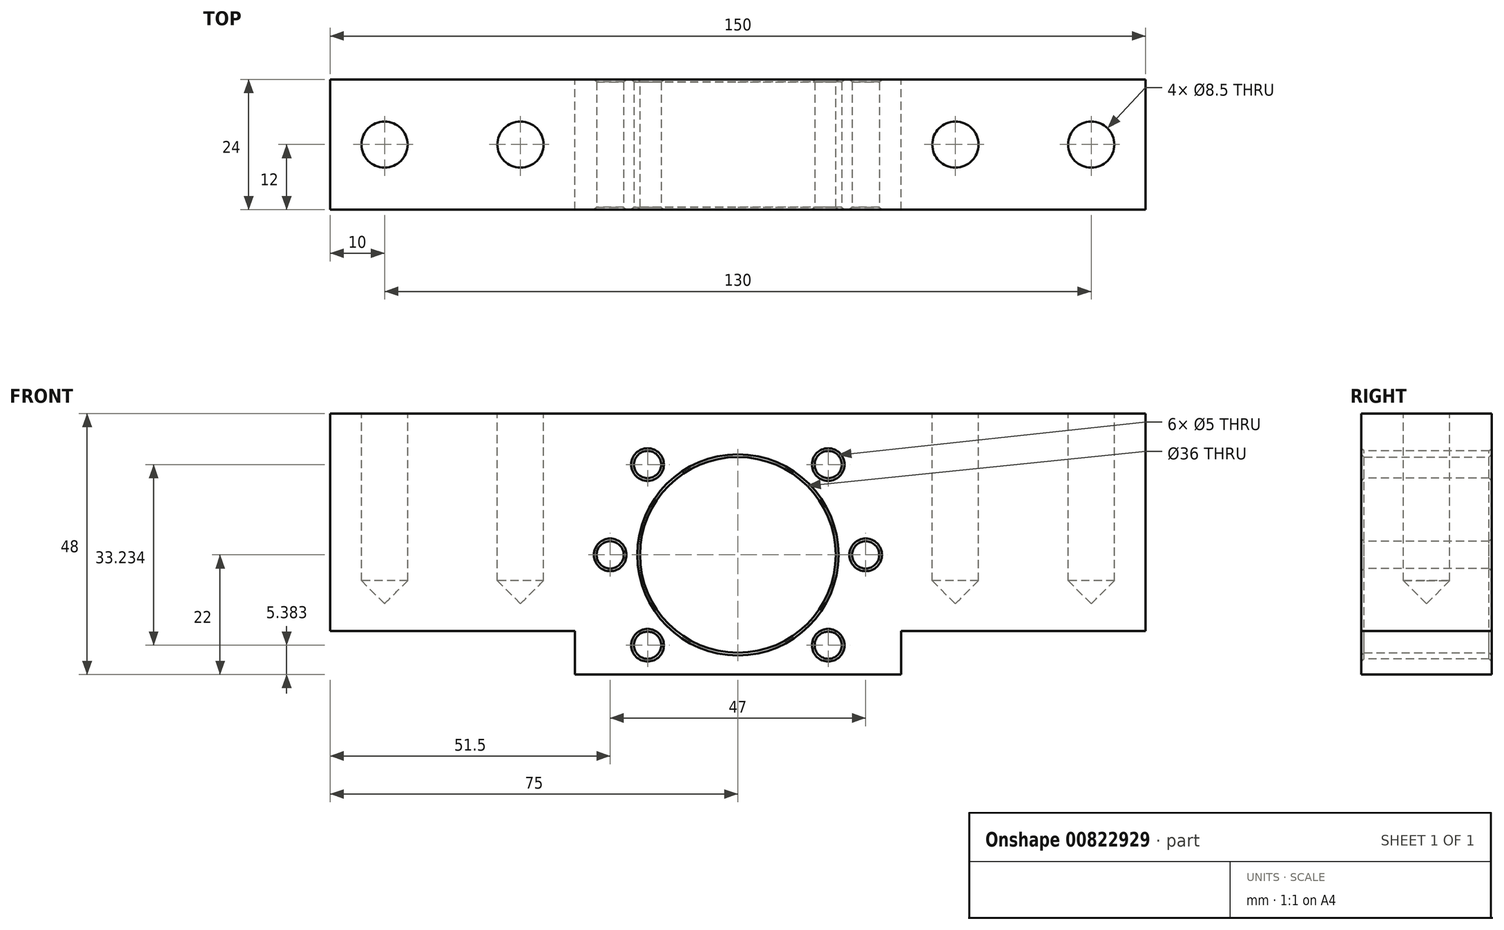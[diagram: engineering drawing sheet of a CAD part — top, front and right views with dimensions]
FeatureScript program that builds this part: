
annotation { "Feature Type Name" : "Feature", "Feature Type Description" : "" }
export const myFeature = defineFeature(function(context is Context, id is Id, definition is map)
    precondition{}
    {
        {
            var Q0;
            Q0=qCreatedBy(makeId("Front.planeOp"),FACE);
            var sketch = newSketch(context, id + "F0", { "sketchPlane" : qUnion([Q0])});
            skCircle(sketch, "E0", {"center": v(0, 0) * mm, "radius": 18 * mm});
            skArc(sketch, "E1", {"start": v(-18.9, 22) * mm, "mid": v(-29, 0) * mm, "end": v(-18.9, -22) * mm, "construction": true});
            skLineSegment(sketch, "E2", {"start": v(0, 0) * mm, "end": v(0, 12) * mm, "construction": true});
            skLineSegment(sketch, "E3", {"start": v(0, 12) * mm, "end": v(-93.5, 12) * mm, "construction": true});
            skLineSegment(sketch, "E4", {"start": v(-93.5, 36) * mm, "end": v(34.56, 36) * mm, "construction": true});
            skLineSegment(sketch, "E5", {"start": v(-93.5, 36) * mm, "end": v(-93.5, 12) * mm, "construction": true});
            skLineSegment(sketch, "E6", {"start": v(-105.7, -10) * mm, "end": v(69, -10) * mm, "construction": true});
            skCircle(sketch, "E7", {"center": v(0, 0) * mm, "radius": 10 * mm, "construction": true});
            skLineSegment(sketch, "E8.bottom", {"start": v(18.9, -22) * mm, "end": v(-18.9, -22) * mm, "construction": true});
            skLineSegment(sketch, "E8.top", {"start": v(18.9, 22) * mm, "end": v(-18.9, 22) * mm, "construction": true});
            skArc(sketch, "E9.trimOffspring", {"start": v(18.9, -22) * mm, "mid": v(29, 0) * mm, "end": v(18.9, 22) * mm, "construction": true});
            skPoint(sketch, "E10.orphan", {"position": v(29, 22) * mm});
            skLineSegment(sketch, "E11.bottom", {"start": v(30, -22) * mm, "end": v(-30, -22) * mm});
            skLineSegment(sketch, "E11.top", {"start": v(30, 30) * mm, "end": v(-30, 30) * mm, "construction": true});
            skLineSegment(sketch, "E11.left", {"start": v(30, -22) * mm, "end": v(30, 30) * mm, "construction": true});
            skLineSegment(sketch, "E11.right", {"start": v(-30, -22) * mm, "end": v(-30, 30) * mm, "construction": true});
            skPoint(sketch, "E11.middle", {"position": v(0, 4) * mm});
            skLineSegment(sketch, "E12", {"start": v(-30, -22) * mm, "end": v(-75, 26) * mm, "construction": true});
            skLineSegment(sketch, "E13", {"start": v(-75, 26) * mm, "end": v(-75, 50) * mm, "construction": true});
            skLineSegment(sketch, "E14", {"start": v(-75, 50) * mm, "end": v(0, 50) * mm, "construction": true});
            skLineSegment(sketch, "E15.MirrorCS", {"start": v(75, 50) * mm, "end": v(0, 50) * mm, "construction": true});
            skLineSegment(sketch, "E16.MirrorCS", {"start": v(75, 26) * mm, "end": v(75, 50) * mm, "construction": true});
            skLineSegment(sketch, "E17.MirrorCS", {"start": v(30, -22) * mm, "end": v(75, 26) * mm, "construction": true});
            skLineSegment(sketch, "E18", {"start": v(-75, 26) * mm, "end": v(75, 26) * mm});
            skLineSegment(sketch, "E19", {"start": v(-75, 26) * mm, "end": v(-75, -14) * mm});
            skLineSegment(sketch, "E20", {"start": v(-75, -14) * mm, "end": v(-30, -14) * mm});
            skLineSegment(sketch, "E21", {"start": v(75, -14) * mm, "end": v(75, 26) * mm});
            skLineSegment(sketch, "E22", {"start": v(-30, -22) * mm, "end": v(-30, -14) * mm});
            skLineSegment(sketch, "E23", {"start": v(30, -22) * mm, "end": v(30, -14) * mm});
            skLineSegment(sketch, "E24.trimOffspring", {"start": v(-25.4, -14) * mm, "end": v(25.4, -14) * mm, "construction": true});
            skLineSegment(sketch, "E25.trimOffspring", {"start": v(30, -14) * mm, "end": v(75, -14) * mm});
            skSolve(sketch);
        }
        {
            var Q0;
            Q0=qSketchRegion(id+"F0",true);
            extrude(context, id + "F1", {"entities" : qUnion([Q0]), "depth" : 24 * mm, "offsetDistance" : 25 * mm});
        }
        {
            var Q0;
            Q0=makeQuery(id+"F1.opExtrude","CAP_FACE",FACE,{"disambiguationData":[OSD([sQuery(id+"F0.wireOp",EDGE,"E0"),sQuery(id+"F0.wireOp",EDGE,"E11.bottom"),sQuery(id+"F0.wireOp",EDGE,"E12"),sQuery(id+"F0.wireOp",EDGE,"E13"),sQuery(id+"F0.wireOp",EDGE,"E14"),sQuery(id+"F0.wireOp",EDGE,"E15.MirrorCS"),sQuery(id+"F0.wireOp",EDGE,"E16.MirrorCS"),sQuery(id+"F0.wireOp",EDGE,"E17.MirrorCS")])],"isStart":false});
            var sketch = newSketch(context, id + "F2", { "sketchPlane" : qUnion([Q0])});
            skLineSegment(sketch, "E26", {"start": v(0, 0) * mm, "end": v(0, 38) * mm, "construction": true});
            skCircle(sketch, "E27", {"center": v(0, 0) * mm, "radius": 23.5 * mm, "construction": true});
            skLineSegment(sketch, "E28", {"start": v(0, 0) * mm, "end": v(-28.4, 0) * mm, "construction": true});
            skCircle(sketch, "E29", {"center": v(-23.5, 0) * mm, "radius": 2.5 * mm});
            skCircle(sketch, "E30.1.0", {"center": v(-16.62, -16.62) * mm, "radius": 2.5 * mm});
            skCircle(sketch, "E30.2.0", {"center": v(0, -23.5) * mm, "radius": 2.5 * mm, "construction": true});
            skCircle(sketch, "E30.3.0", {"center": v(16.62, -16.62) * mm, "radius": 2.5 * mm});
            skCircle(sketch, "E30.4.0", {"center": v(23.5, 0) * mm, "radius": 2.5 * mm});
            skCircle(sketch, "E30.5.0", {"center": v(16.62, 16.62) * mm, "radius": 2.5 * mm});
            skCircle(sketch, "E30.6.0", {"center": v(0, 23.5) * mm, "radius": 2.5 * mm, "construction": true});
            skCircle(sketch, "E30.7.0", {"center": v(-16.62, 16.62) * mm, "radius": 2.5 * mm});
            skCircle(sketch, "E31", {"center": v(0, 0) * mm, "radius": 30 * mm, "construction": true});
            skSolve(sketch);
        }
        {
            var Q0;
            Q0=qSketchRegion(id+"F2",true);
            extrude(context, id + "F3", {"entities" : qUnion([Q0]), "operationType" : NewBodyOperationType.REMOVE, "oppositeDirection" : true, "depth" : 25 * mm, "offsetDistance" : 25 * mm});
        }
        {
            var Q0;
            Q0=makeQuery(id+"F1.opExtrude","SWEPT_FACE",FACE,{"disambiguationData":[OSD([sQuery(id+"F0.wireOp",EDGE,"E18")])]});
            var sketch = newSketch(context, id + "F4", { "sketchPlane" : qUnion([Q0])});
            skLineSegment(sketch, "E32.0.0", {"start": v(75, 0) * mm, "end": v(-75, 0) * mm, "construction": true});
            skLineSegment(sketch, "E32.0.1", {"start": v(-75, 0) * mm, "end": v(-75, -24) * mm, "construction": true});
            skLineSegment(sketch, "E32.0.2", {"start": v(-75, -24) * mm, "end": v(75, -24) * mm, "construction": true});
            skLineSegment(sketch, "E32.0.3", {"start": v(75, -24) * mm, "end": v(75, 0) * mm, "construction": true});
            skLineSegment(sketch, "E33", {"start": v(-75, -12) * mm, "end": v(75, -12) * mm, "construction": true});
            skLineSegment(sketch, "E34.0", {"start": v(-30, -24) * mm, "end": v(-30, 0) * mm, "construction": true});
            skLineSegment(sketch, "E35.0", {"start": v(30, -24) * mm, "end": v(30, 0) * mm, "construction": true});
            skPoint(sketch, "E36.0", {"position": v(0, 0) * mm});
            skLineSegment(sketch, "E37", {"start": v(0, 0) * mm, "end": v(0, -24) * mm, "construction": true});
            skCircle(sketch, "E38", {"center": v(-65, -12) * mm, "radius": 4.25 * mm});
            skCircle(sketch, "E39", {"center": v(-40, -12) * mm, "radius": 4.25 * mm});
            skCircle(sketch, "E40.MirrorC", {"center": v(65, -12) * mm, "radius": 4.25 * mm});
            skCircle(sketch, "E41.MirrorC", {"center": v(40, -12) * mm, "radius": 4.25 * mm});
            skCircle(sketch, "E42", {"center": v(-65, -12) * mm, "radius": 9 * mm, "construction": true});
            skCircle(sketch, "E43", {"center": v(-40, -12) * mm, "radius": 9 * mm, "construction": true});
            skSolve(sketch);
        }
        {
            var Q0;
            Q0 = qSketchRegion(id + "F4", true);
            extrude(context, id + "F5", {"entities" : qUnion([Q0]), "operationType" : NewBodyOperationType.REMOVE, "oppositeDirection" : true, "depth" : 35 * mm, "offsetDistance" : 25 * mm});
        }
        {
            var Q0;
            Q0=makeQuery(id+"F5.boolean.opBoolean","COPY",FACE,{"derivedFrom":makeQuery(id+"F5.opExtrude","CAP_FACE",FACE,{"disambiguationData":[OSD([sQuery(id+"F4.wireOp",EDGE,"E38")])],"isStart":false})});
            var Q1;
            Q1=makeQuery(id+"F5.boolean.opBoolean","COPY",FACE,{"derivedFrom":makeQuery(id+"F5.opExtrude","CAP_FACE",FACE,{"disambiguationData":[OSD([sQuery(id+"F4.wireOp",EDGE,"E39")])],"isStart":false})});
            var Q2;
            Q2=makeQuery(id+"F5.boolean.opBoolean","COPY",FACE,{"derivedFrom":makeQuery(id+"F5.opExtrude","CAP_FACE",FACE,{"disambiguationData":[OSD([sQuery(id+"F4.wireOp",EDGE,"E41.MirrorC")])],"isStart":false})});
            var Q3;
            Q3=makeQuery(id+"F5.boolean.opBoolean","COPY",FACE,{"derivedFrom":makeQuery(id+"F5.opExtrude","CAP_FACE",FACE,{"disambiguationData":[OSD([sQuery(id+"F4.wireOp",EDGE,"E40.MirrorC")])],"isStart":false})});
            chamfer(context, id + "F6", {"entities" : qUnion([Q0, Q1, Q2, Q3]), "width" : 4.25 * mm, "tangentPropagation" : true});
        }
        {
            var Q0;
            Q0=makeQuery(id+"F5.boolean.opBoolean","COPY",EDGE,{"derivedFrom":makeQuery(id+"F5.opExtrude","CAP_EDGE",EDGE,{"disambiguationData":[OSD([sQuery(id+"F4.wireOp",EDGE,"E38")])],"isStart":true})});
            var Q1;
            Q1=makeQuery(id+"F5.boolean.opBoolean","COPY",EDGE,{"derivedFrom":makeQuery(id+"F5.opExtrude","CAP_EDGE",EDGE,{"disambiguationData":[OSD([sQuery(id+"F4.wireOp",EDGE,"E39")])],"isStart":true})});
            var Q2;
            Q2=makeQuery(id+"F5.boolean.opBoolean","COPY",EDGE,{"derivedFrom":makeQuery(id+"F5.opExtrude","CAP_EDGE",EDGE,{"disambiguationData":[OSD([sQuery(id+"F4.wireOp",EDGE,"E41.MirrorC")])],"isStart":true})});
            var Q3;
            Q3=makeQuery(id+"F5.boolean.opBoolean","COPY",EDGE,{"derivedFrom":makeQuery(id+"F5.opExtrude","CAP_EDGE",EDGE,{"disambiguationData":[OSD([sQuery(id+"F4.wireOp",EDGE,"E40.MirrorC")])],"isStart":true})});
            var Q4;
            Q4=makeQuery(id+"F1.opExtrude","SWEPT_FACE",FACE,{"disambiguationData":[OSD([sQuery(id+"F0.wireOp",EDGE,"E0")])]});
            var Q5;
            Q5=makeQuery(id+"F3.boolean.opBoolean","COPY",FACE,{"derivedFrom":makeQuery(id+"F3.opExtrude","SWEPT_FACE",FACE,{"disambiguationData":[OSD([sQuery(id+"F2.wireOp",EDGE,"E29")])]})});
            var Q6;
            Q6=makeQuery(id+"F3.boolean.opBoolean","COPY",FACE,{"derivedFrom":makeQuery(id+"F3.opExtrude","SWEPT_FACE",FACE,{"disambiguationData":[OSD([sQuery(id+"F2.wireOp",EDGE,"E30.7.0")])]})});
            var Q7;
            Q7=makeQuery(id+"F3.boolean.opBoolean","COPY",FACE,{"derivedFrom":makeQuery(id+"F3.opExtrude","SWEPT_FACE",FACE,{"disambiguationData":[OSD([sQuery(id+"F2.wireOp",EDGE,"E30.1.0")])]})});
            var Q8;
            Q8=makeQuery(id+"F3.boolean.opBoolean","COPY",FACE,{"derivedFrom":makeQuery(id+"F3.opExtrude","SWEPT_FACE",FACE,{"disambiguationData":[OSD([sQuery(id+"F2.wireOp",EDGE,"E30.3.0")])]})});
            var Q9;
            Q9=makeQuery(id+"F3.boolean.opBoolean","COPY",FACE,{"derivedFrom":makeQuery(id+"F3.opExtrude","SWEPT_FACE",FACE,{"disambiguationData":[OSD([sQuery(id+"F2.wireOp",EDGE,"E30.4.0")])]})});
            var Q10;
            Q10=makeQuery(id+"F3.boolean.opBoolean","COPY",FACE,{"derivedFrom":makeQuery(id+"F3.opExtrude","SWEPT_FACE",FACE,{"disambiguationData":[OSD([sQuery(id+"F2.wireOp",EDGE,"E30.5.0")])]})});
            chamfer(context, id + "F7", {"entities" : qUnion([Q0, Q1, Q2, Q3, Q4, Q5, Q6, Q7, Q8, Q9, Q10]), "width" : 0.5 * mm, "tangentPropagation" : true});
        }
    });
